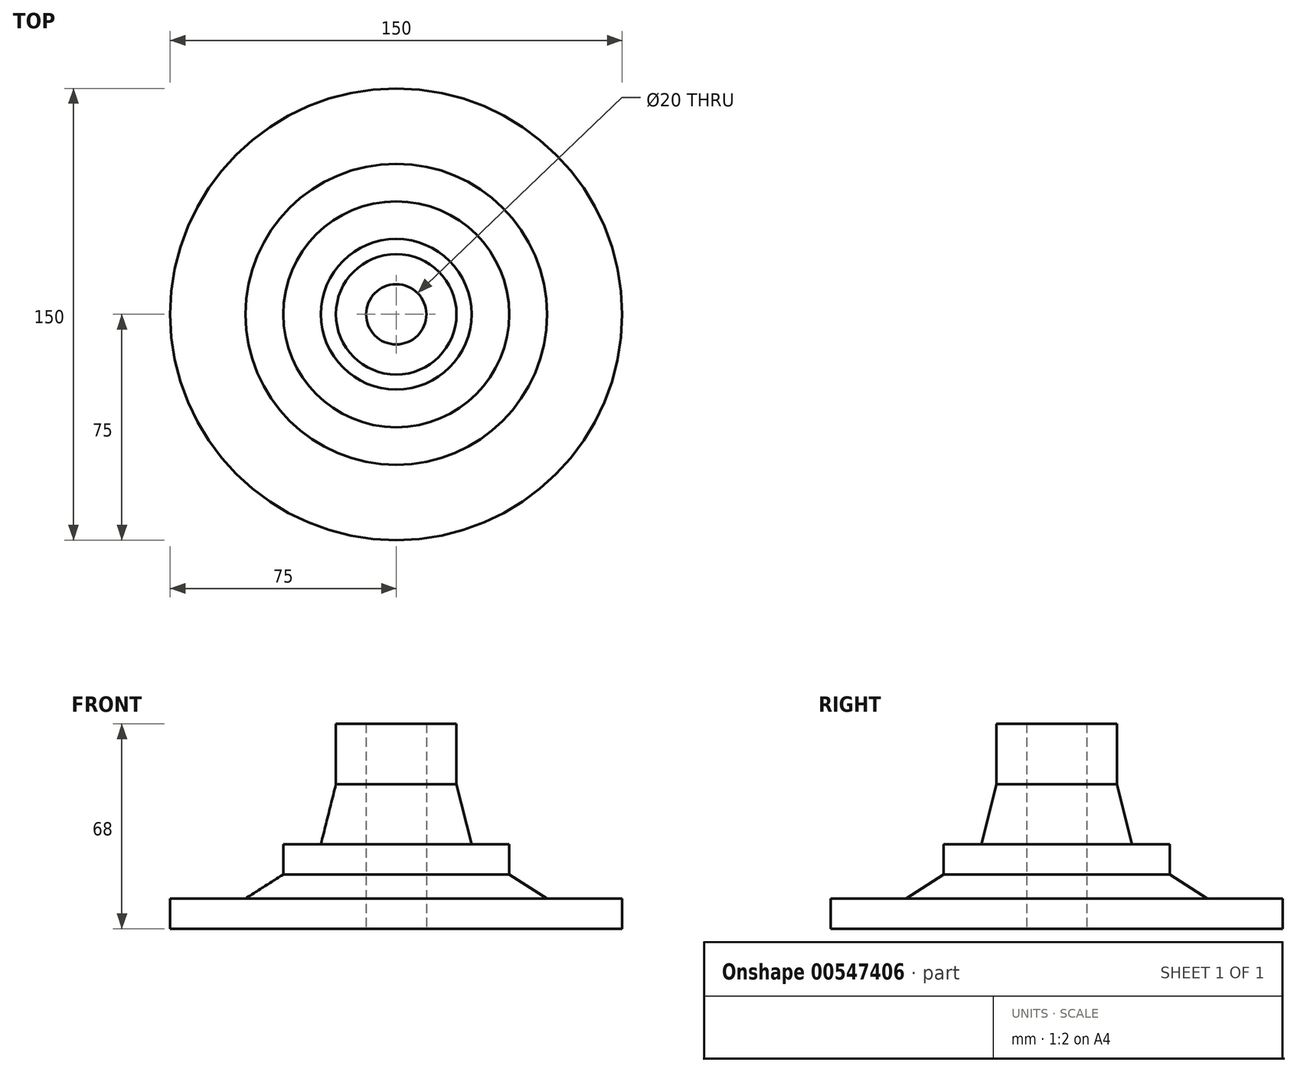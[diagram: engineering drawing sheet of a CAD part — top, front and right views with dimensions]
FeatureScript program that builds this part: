
annotation { "Feature Type Name" : "Feature", "Feature Type Description" : "" }
export const myFeature = defineFeature(function(context is Context, id is Id, definition is map)
    precondition{}
    {
        {
            var Q0;
            Q0=qCreatedBy(makeId("Front.planeOp"),FACE);
            var sketch = newSketch(context, id + "F0", { "sketchPlane" : qUnion([Q0])});
            skLineSegment(sketch, "E0", {"start": v(0, 0) * mm, "end": v(0, 73.16) * mm});
            skLineSegment(sketch, "E1", {"start": v(-10, 0) * mm, "end": v(-10, 68) * mm});
            skLineSegment(sketch, "E2", {"start": v(-10, 68) * mm, "end": v(-20, 68) * mm});
            skLineSegment(sketch, "E3", {"start": v(-20, 68) * mm, "end": v(-20, 48) * mm});
            skLineSegment(sketch, "E4", {"start": v(-20, 48) * mm, "end": v(-25, 28) * mm});
            skLineSegment(sketch, "E5", {"start": v(-25, 28) * mm, "end": v(-37.5, 28) * mm});
            skLineSegment(sketch, "E6", {"start": v(-37.5, 28) * mm, "end": v(-37.5, 18) * mm});
            skLineSegment(sketch, "E7", {"start": v(-37.5, 18) * mm, "end": v(-50, 10) * mm});
            skLineSegment(sketch, "E8", {"start": v(-50, 10) * mm, "end": v(-75, 10) * mm});
            skLineSegment(sketch, "E9", {"start": v(-75, 10) * mm, "end": v(-75, 0) * mm});
            skLineSegment(sketch, "E10", {"start": v(-75, 0) * mm, "end": v(-10, 0) * mm});
            skSolve(sketch);
        }
        {
            var Q0;
            Q0=qSketchRegion(id+"F0",true);
            var Q1;
            Q1=sQuery(id+"F0.wireOp",EDGE,"E0");
            revolve(context, id + "F1", {"entities" : qUnion([Q0]), "axis" : qUnion([Q1]), "revolveType" : RevolveType.FULL});
        }
    });
